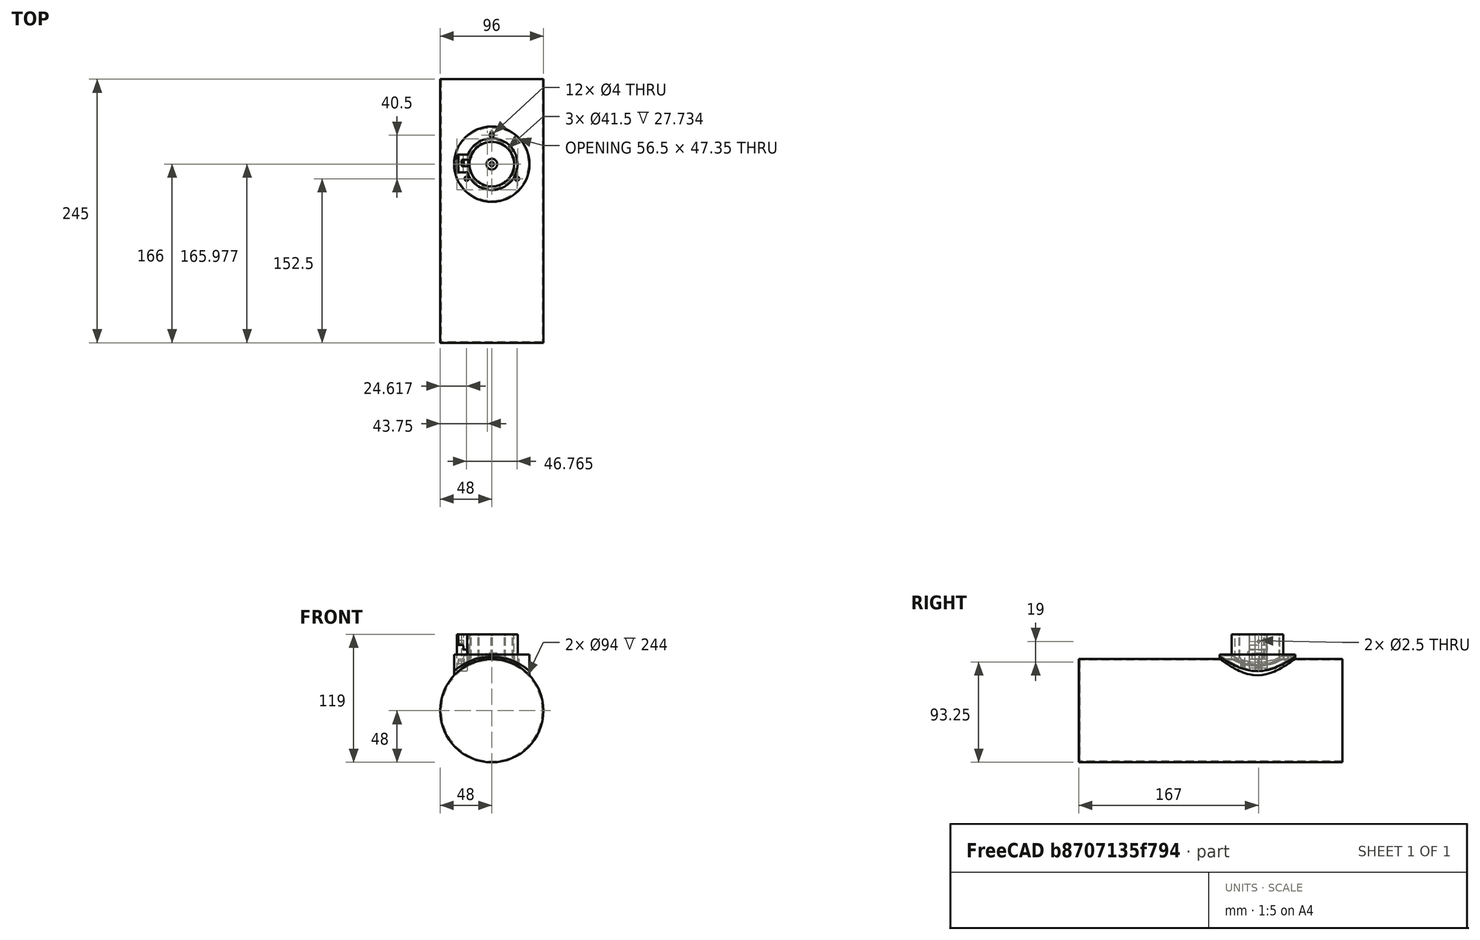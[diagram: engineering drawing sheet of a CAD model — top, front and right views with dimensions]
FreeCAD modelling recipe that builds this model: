
FCSTD DOCUMENT  (FreeCAD 0.14R3702 (Git))
Label: Partes telescopio
License: CC-BY 3.0
LicenseURL: http://creativecommons.org/licenses/by/3.0/
objects: Part::Cut×23, Part::Cylinder×20, Part::Box×7, Part::Fuse×6, App::DocumentObjectGroup×4, Part::FeaturePython×4, Part::MultiFuse×2, Part::Fillet×2
note: 64 computed .brp shape members not serialized (recipe doc carries the construction recipe); baked Part::Feature solids carry a one-line shape summary decoded from their .brp

FEATURE [Part::Cylinder] Cylinder  label="Bumper"
  Angle = 360
  Height = 6.4
  Radius = 5
FEATURE [Part::Cylinder] Cylinder001  label="Bumper taladro"
  Angle = 360
  Height = 6.4
  Radius = 2
FEATURE [Part::Cut] Cut  label="Bumper sin telescopio"
  Base = -> Cylinder
  Tool = -> Cylinder001
FEATURE [Part::Cylinder] Cylinder003  label="Cilindro"
  Angle = 360
  Height = 245
  Placement = pos=(0,79,-47) rot=(1,0,0;1.5708rad)
  Radius = 48
FEATURE [Part::Cut] Cut001  label="Bumper para m2 - temporal"
  Base = -> Cut
  Tool = -> Cylinder003
FEATURE [App::DocumentObjectGroup] Grupo002  label="Bumper para m2"
  Group = -> [Cut001]
FEATURE [App::DocumentObjectGroup] Grupo001  label="Temporales"
  Group = -> [Grupo002]
FEATURE [Part::Cylinder] Cylinder005  label="Cilindro externo metálico"
  Angle = 360
  Height = 245
  Placement = pos=(0,79,-47) rot=(1,0,0;1.5708rad)
  Radius = 48
FEATURE [App::DocumentObjectGroup] Grupo003  label="Enfocador para DSLR nikon"
  Group = -> [Cylinder005]
FEATURE [Part::Cylinder] Cylinder006  label="Taladro para luz m2 a enfocador"
  Angle = 360
  Height = 20
  Placement = pos=(0,0,-12) rot=(0,0,1;0rad)
  Radius = 22.5
FEATURE [Part::Cut] Cut003  label="Cilindro metálico con taladro para luz de m2"
  Tool = -> Cylinder006
FEATURE [Part::Box] Box  label="Taladro cubo para engranaje enfocador"
  Height = 10
  Length = 6
  Placement = pos=(-28,-2,-9) rot=(0,0,1;0rad)
  Width = 6
FEATURE [Part::Cut] Cut004  label="Cilindro metálico base"
  Base = -> Cut003
  Tool = -> Box
FEATURE [Part::Cylinder] Cylinder008  label="Taladro para repetición axial"
  Angle = 360
  Height = 20
  Placement = pos=(0,27,-10) rot=(0,0,1;0rad)
  Radius = 2
FEATURE [App::DocumentObjectGroup] Grupo  label="Partes telescopio"
  Group = -> [Grupo001,Grupo003,Cylinder008,Cylinder006]
FEATURE [Part::FeaturePython] Array  label="Taladros para cilindro metálico base"  # Draft array (typed FeaturePython)
  Angle = 360
  ArrayType = 1
  Axis = (0,0,1)
  Base = -> Cylinder008
  Center = (0,0,0)
  IntervalX = (1,0,0)
  IntervalY = (0,1,0)
  IntervalZ = (0,0,1)
  NumberPolar = 3
  NumberX = 2
  NumberY = 2
  NumberZ = 1
FEATURE [Part::Cut] Cut005  label="Base telescopio"
  Base = -> Cut004
  Tool = -> Array
FEATURE [Part::Box] Box001  label="Taladro cubo para engranaje, a cilindro"
  Height = 120
  Length = 6
  Placement = pos=(-28,-2,-10) rot=(0,0,1;0rad)
  Width = 6
FEATURE [Part::Cylinder] Cylinder009  label="Taladro para luz m2 a enfocador, cilindro exterior"
  Angle = 360
  Height = 150
  Placement = pos=(0,0,-32) rot=(0,0,1;0rad)
  Radius = 20.75
FEATURE [Part::Cylinder] Cylinder010  label="Taladro para repetición axial001"
  Angle = 360
  Height = 40
  Placement = pos=(0,27,-30) rot=(0,0,1;0rad)
  Radius = 2
FEATURE [Part::FeaturePython] Array001  label="Repetición axial de taladro en cilindro metálico"  # Draft array (typed FeaturePython)
  Angle = 360
  ArrayType = 1
  Axis = (0,0,1)
  Base = -> Cylinder010
  Center = (0,0,0)
  IntervalX = (1,0,0)
  IntervalY = (0,1,0)
  IntervalZ = (0,0,1)
  NumberPolar = 3
  NumberX = 2
  NumberY = 2
  NumberZ = 1
FEATURE [Part::Cylinder] Cylinder011  label="Exterior de base de enfocador"
  Angle = 360
  Height = 30
  Placement = pos=(0,0,-25) rot=(0,0,1;0rad)
  Radius = 35
FEATURE [Part::Cylinder] Cylinder012  label="Cilindro externo metálico, taladro a base enfocador"
  Angle = 360
  Height = 245
  Placement = pos=(0,79,-47) rot=(1,0,0;1.5708rad)
  Radius = 48
FEATURE [Part::Cylinder] Cylinder013  label="Cilindro externo de enfocador"
  Angle = 360
  Height = 56
  Placement = pos=(0,0,-32) rot=(0,0,1;0rad)
  Radius = 24
FEATURE [Part::Cylinder] Cylinder014  label="Cilindro externo, taladro para base enfocador"
  Angle = 360
  Height = 245
  Placement = pos=(0,79,-47) rot=(1,0,0;1.5708rad)
  Radius = 48
FEATURE [Part::Cut] Cut008  label="Cilindro exterior con corte de base de telescopio"
  Base = -> Cylinder013
  Tool = -> Cylinder014
FEATURE [Part::Cut] Cut009  label="Cilindro exterior con base y taladro para luz m2"
  Base = -> Cut008
  Tool = -> Cylinder009
FEATURE [Part::Cylinder] Cylinder015  label="Taladro para luz m2 a enfocador, base enfocador"
  Angle = 360
  Height = 150
  Placement = pos=(0,0,-32) rot=(0,0,1;0rad)
  Radius = 22.5
FEATURE [Part::Box] Box002  label="Cubo externo para riel de enfocador"
  Height = 34
  Length = 10
  Placement = pos=(-32.5,-7.5,-10) rot=(0,0,1;0rad)
  Width = 16.5
FEATURE [Part::Fuse] Fusion002  label="Enfocador base, cilindro y externo para riel"
  Tool = -> Box002
FEATURE [Part::Cut] Cut011  label="Enfocador base, cilindro y riel externo sin corte telescopio"
  Base = -> Fusion002
  Tool = -> Box001
FEATURE [Part::Fuse] Fusion003
  Tool = -> Box002
FEATURE [Part::Cut] Cut013  label="Cilindro metálico base001"
  Base = -> Cut003
  Tool = -> Box
FEATURE [Part::Cut] Cut014  label="Base enfocador con taladro para riel para engranaje"
  Base = -> Cut011
  Tool = -> Cylinder005
FEATURE [Part::Fuse] Fusion005
  Tool = -> Box002
FEATURE [Part::Cylinder] Cylinder016  label="Cilindro externo, taladro de enfocador"
  Angle = 360
  Height = 245
  Placement = pos=(0,79,-47) rot=(1,0,0;1.5708rad)
  Radius = 48
FEATURE [Part::Fuse] Fusion007
  Tool = -> Box002
FEATURE [Part::Box] Box003  label="Taladro cubo para engranaje, a cilindro001"
  Height = 120
  Length = 6
  Placement = pos=(-26,-2,-10) rot=(0,0,1;0rad)
  Width = 6
FEATURE [Part::Cylinder] Cylinder017  label="Cilindro interno para forma curva en base"
  Angle = 360
  Height = 245
  Placement = pos=(0,79,-47) rot=(1,0,0;1.5708rad)
  Radius = 51
FEATURE [Part::Cylinder] Cylinder018  label="Cilindro externo para forma curva en base"
  Angle = 360
  Height = 245
  Placement = pos=(0,79,-47) rot=(1,0,0;1.5708rad)
  Radius = 65
FEATURE [Part::Cut] Cut015  label="Cilindro hueco, taladro para corte de forma de base"
  Base = -> Cylinder018
  Tool = -> Cylinder017
FEATURE [Part::Cut] Cut016  label="Base enfocador con corte superior"
  Base = -> Cylinder011
  Tool = -> Cut015
FEATURE [Part::Cut] Cut017  label="Base enfocador con corte superior e inferior"
  Base = -> Cut016
  Tool = -> Cylinder012
FEATURE [Part::Cut] Cut018  label="Base enfocador con contorno y taladores de tornillos"
  Base = -> Cut017
  Tool = -> Array001
FEATURE [Part::Cut] Cut019  label="Base enfocador con taladros de m2, tornillos y contorno"
  Base = -> Cut018
  Tool = -> Cylinder015
FEATURE [Part::Fuse] Fusion  label="Cilindro de enfocador con cubo de riel"
  Base = -> Cut009
  Tool = -> Box002
FEATURE [Part::MultiFuse] Fusion008  label="Base enfocador con cilindro y cubo de riel"
  Shapes = -> [Cut019,Fusion]
FEATURE [Part::Cut] Cut020  label="Enfocador con taladro de riel"
  Base = -> Fusion008
  Tool = -> Box003
FEATURE [Part::Cylinder] Cylinder019  label="Taladro de riel de engranaje manual"
  Angle = 360
  Height = 20
  Placement = pos=(-25,10,7) rot=(1,0,0;1.5708rad)
  Radius = 2.75
FEATURE [Part::Fuse] Fusion009
  Base = -> Cut009
  Tool = -> Box002
FEATURE [Part::Cut] Cut021  label="Enfocador con taladro de riel de engranaje manual"
  Base = -> Cut020
  Tool = -> Cylinder019
FEATURE [Part::Box] Box004  label="Cubo taladro para riel de engranaje manual"
  Height = 13
  Length = 5.5
  Placement = pos=(-32,-9,1) rot=(0,0,1;0rad)
  Width = 19
FEATURE [Part::Cut] Cut022  label="Enfocador con taladro en cubo para riel manual"
  Base = -> Cut021
  Tool = -> Box004
FEATURE [Part::Box] Box005  label="Cubo taladro para ajuste de altura de enfocador manual"
  Height = 28
  Length = 10
  Placement = pos=(-41,-8,-4) rot=(0,0,1;0rad)
  Width = 18
FEATURE [Part::Cut] Cut023  label="Enfocador con ajuste de altura de enfocador manual"
  Base = -> Cut022
  Tool = -> Box005
FEATURE [Part::Box] Box006  label="Cubo taladro para pase engranaje manual de enfocador"
  Height = 12
  Length = 10
  Width = 6
FEATURE [Part::Cut] Cut024  label="Base enfocador con base para engranaje"
  Base = -> Cut023
  Tool = -> Box006
FEATURE [Part::Cylinder] Cylinder020  label="Taladro para tornillo pequeño en enfocador manual"
  Angle = 360
  Height = 10
  Placement = pos=(-35,1,-1.75) rot=(0,1,0;1.5708rad)
  Radius = 1.25
FEATURE [Part::FeaturePython] Array002  label="Taladros para tornillo pequeño en array de Z"  # Draft array (typed FeaturePython)
  Angle = 360
  ArrayType = 0
  Axis = (0,0,1)
  Base = -> Cylinder020
  Center = (0,0,0)
  IntervalX = (1,0,0)
  IntervalY = (0,1,0)
  IntervalZ = (0,0,19)
  NumberPolar = 2
  NumberX = 1
  NumberY = 1
  NumberZ = 2
FEATURE [Part::Cut] Cut025  label="Base enfocador sin redondeos"
  Base = -> Cut024
  Tool = -> Array002
FEATURE [Part::Fillet] Fillet  label="Redondeo de base"
  Base = -> Cut025
  Edges = 1 edges r=1: [Edge3]
FEATURE [Part::Fillet] Fillet001  label="Redondeo interno en base de enfocador manual"
  Base = -> Fillet
  Edges = 2 edges r=1: [Edge108,Edge127]
FEATURE [Part::Cut] Cut026  label="Enfocador con cilindro, base manual y redondeos"
  Base = -> Fillet001
  Tool = -> Cylinder016
FEATURE [Part::Cylinder] Cylinder021  label="Ajuste interno para riel de enfocador"
  Angle = 360
  Height = 21
  Placement = pos=(0,20.7,2) rot=(0,0,1;0rad)
  Radius = 0.5
FEATURE [Part::FeaturePython] Array003  label="Array de ajustes para cilindro interno de enfocador"  # Draft array (typed FeaturePython)
  Angle = 360
  ArrayType = 1
  Axis = (0,0,1)
  Base = -> Cylinder021
  Center = (0,0,0)
  IntervalX = (1,0,0)
  IntervalY = (0,1,0)
  IntervalZ = (0,0,1)
  NumberPolar = 5
  NumberX = 2
  NumberY = 2
  NumberZ = 1
FEATURE [Part::MultiFuse] Fusion010  label="Enfocador con ajustes internos"
  Shapes = -> [Cut026,Array003]
FEATURE [Part::Cylinder] Cylinder022  label="Ajuste para taladro de sosten de m2"
  Angle = 360
  Height = 40
  Placement = pos=(0,29,-30) rot=(0,0,1;0rad)
  Radius = 2
FEATURE [Part::Cut] Cut027  label="Enfocador con ajuste para sosten de m2"
  Base = -> Fusion010
  Tool = -> Cylinder022
